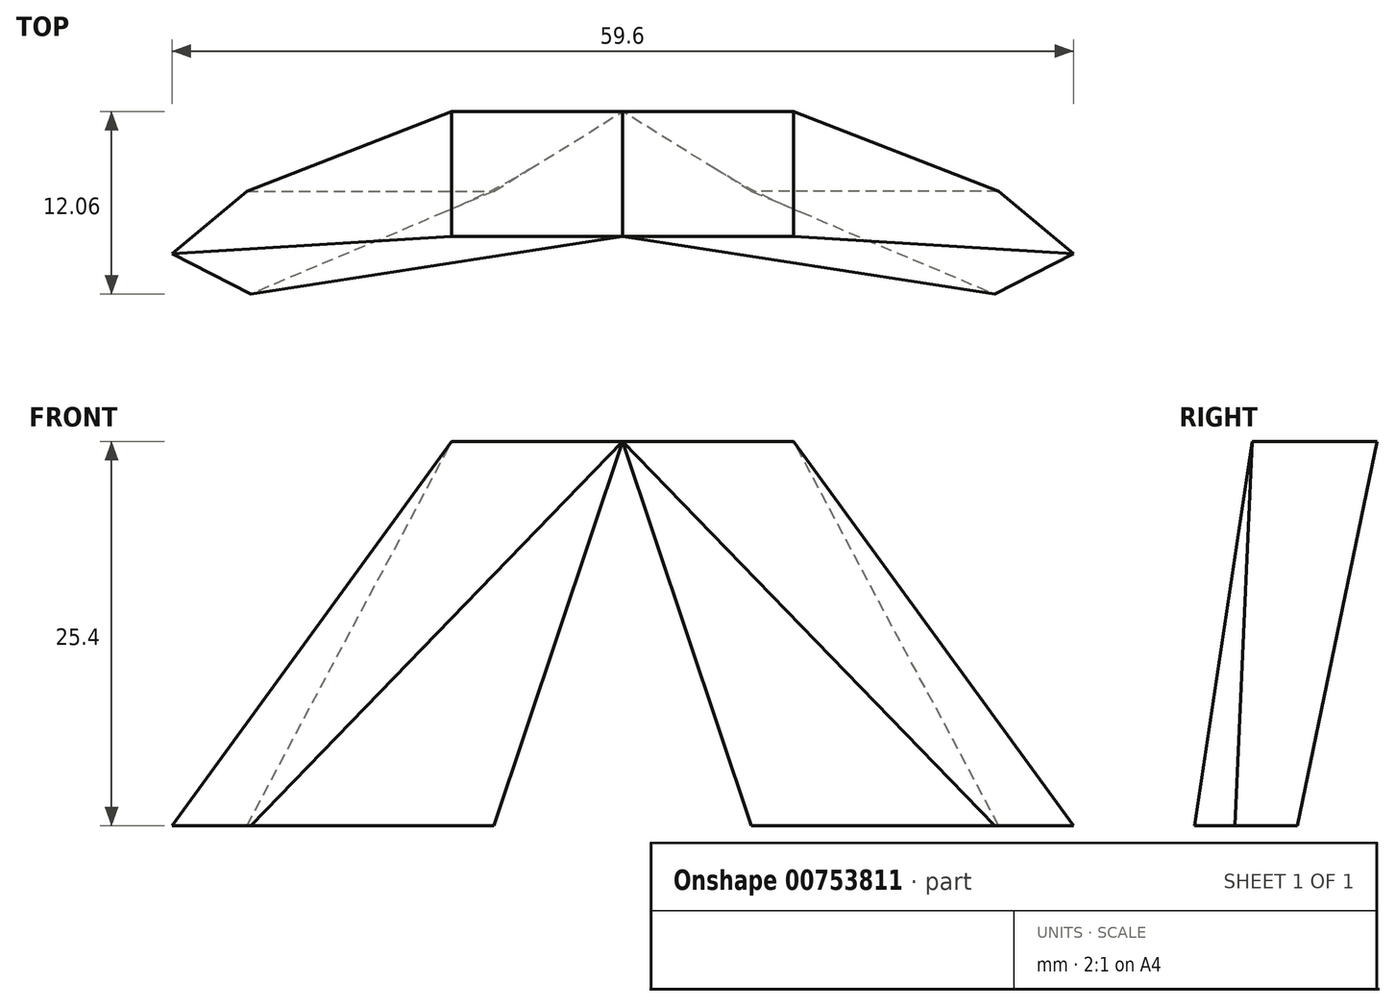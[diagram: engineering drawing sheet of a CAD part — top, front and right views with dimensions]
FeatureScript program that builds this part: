
annotation { "Feature Type Name" : "Feature", "Feature Type Description" : "" }
export const myFeature = defineFeature(function(context is Context, id is Id, definition is map)
    precondition{}
    {
        {
            var Q0;
            Q0=qCreatedBy(makeId("Top.planeOp"),FACE);
            var sketch = newSketch(context, id + "F0", { "sketchPlane" : qUnion([Q0])});
            skPoint(sketch, "E0", {"position": v(24.58, -12.06) * mm});
            skLineSegment(sketch, "E1", {"start": v(8.51, -5.27) * mm, "end": v(8.51, -5.27) * mm});
            skLineSegment(sketch, "E2", {"start": v(24.85, -5.27) * mm, "end": v(8.51, -5.27) * mm});
            skPoint(sketch, "E3", {"position": v(8.51, -5.27) * mm});
            skLineSegment(sketch, "E4", {"start": v(8.51, -5.27) * mm, "end": v(24.58, -12.06) * mm});
            skLineSegment(sketch, "E5", {"start": v(24.58, -12.06) * mm, "end": v(29.8, -9.39) * mm});
            skLineSegment(sketch, "E6", {"start": v(29.8, -9.39) * mm, "end": v(24.85, -5.27) * mm});
            skSolve(sketch);
        }
        {
            var Q0;
            Q0=qCreatedBy(makeId("Top.planeOp"),FACE);
            cPlane(context, id + "F1", {"entities" : qUnion([Q0]), "cplaneType" : CPlaneType.OFFSET, "offset" : 25.4 * mm, "width" : 152.4 * mm, "height" : 152.4 * mm});
        }
        {
            var Q0;
            Q0=qCreatedBy(id+"F1.planeOp",FACE);
            var sketch = newSketch(context, id + "F2", { "sketchPlane" : qUnion([Q0])});
            skLineSegment(sketch, "E7.bottom", {"start": v(0, 0) * mm, "end": v(11.3, 0) * mm});
            skLineSegment(sketch, "E7.top", {"start": v(0, -8.25) * mm, "end": v(11.3, -8.25) * mm});
            skLineSegment(sketch, "E7.left", {"start": v(0, 0) * mm, "end": v(0, -8.25) * mm});
            skLineSegment(sketch, "E7.right", {"start": v(11.3, 0) * mm, "end": v(11.3, -8.25) * mm});
            skPoint(sketch, "E7.middle", {"position": v(5.65, -4.12) * mm});
            skSolve(sketch);
        }
        {
            var Q0;
            Q0=makeQuery(id+"F0.imprint","IMPRINT",FACE,{"disambiguationData":[TD([[makeQuery(id+"F0.imprint","IMPRINT",EDGE,{"derivedFrom":sQuery(id+"F0.wireOp",EDGE,"E2")}),1.0]])]});
            var Q1;
            Q1=makeQuery(id+"F2.imprint","IMPRINT",FACE,{"disambiguationData":[TD([[makeQuery(id+"F2.imprint","IMPRINT",EDGE,{"derivedFrom":sQuery(id+"F2.wireOp",EDGE,"E7.bottom")}),-1.0]])]});
            loft(context, id + "F3", {"sheetProfilesArray" : [{ "sheetProfileEntities" : qUnion([Q0]) }, { "sheetProfileEntities" : qUnion([Q1]) }]});
        }
        {
            var Q0;
            Q0=makeQuery(id+"F3.opLoft","SWEPT_BODY",BODY,{"disambiguationData":[OSD([makeQuery(id+"F0.imprint","IMPRINT",FACE,{"disambiguationData":[TD([[makeQuery(id+"F0.imprint","IMPRINT",EDGE,{"derivedFrom":sQuery(id+"F0.wireOp",EDGE,"E2")}),1.0]])]}),makeQuery(id+"F2.imprint","IMPRINT",FACE,{"disambiguationData":[TD([[makeQuery(id+"F2.imprint","IMPRINT",EDGE,{"derivedFrom":sQuery(id+"F2.wireOp",EDGE,"E7.bottom")}),-1.0]])]})])]});
            var Q1;
            Q1=qCreatedBy(makeId("Right.planeOp"),FACE);
            mirror(context, id + "F4", {"entities" : qUnion([Q0]), "mirrorPlane" : qUnion([Q1])});
        }
    });
